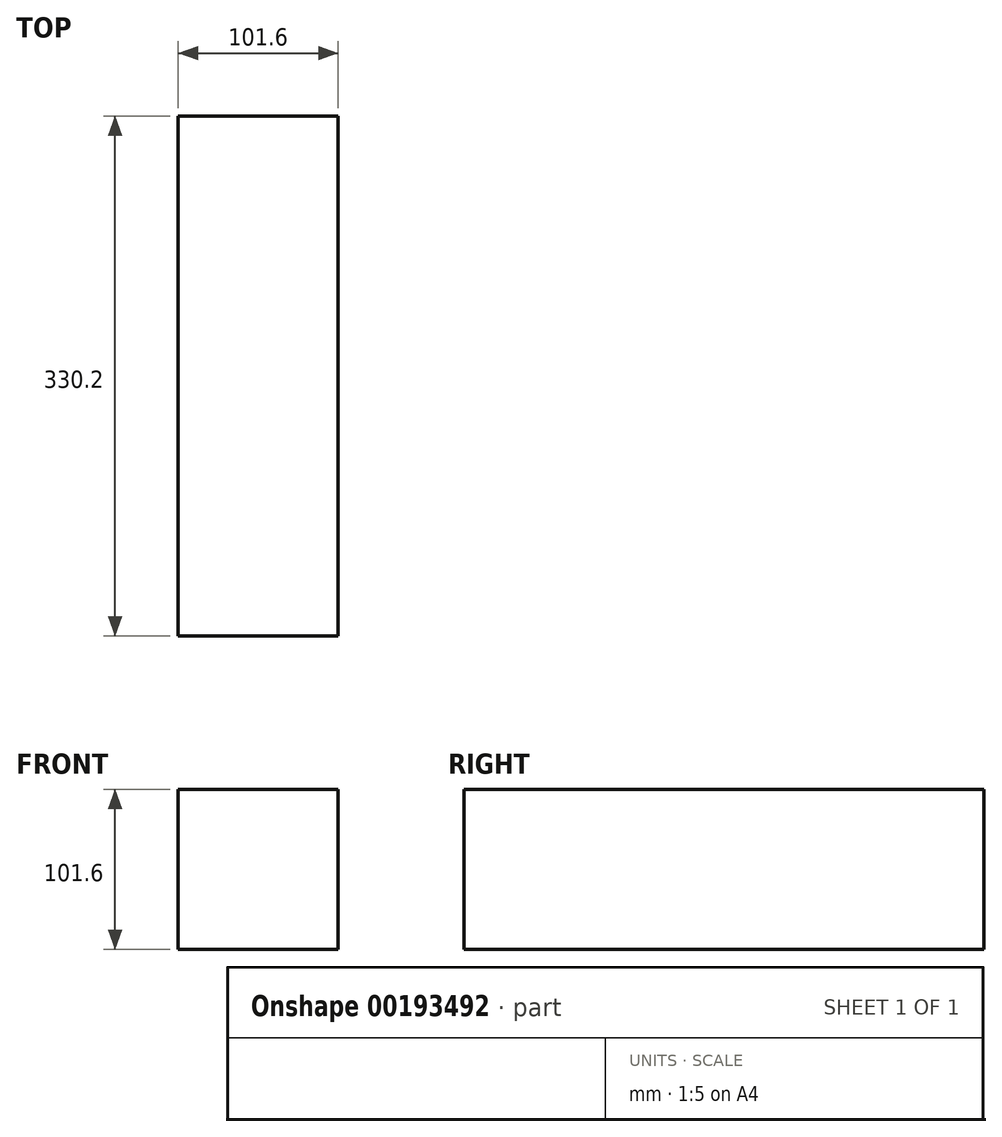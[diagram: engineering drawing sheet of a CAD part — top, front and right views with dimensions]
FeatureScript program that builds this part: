
annotation { "Feature Type Name" : "Feature", "Feature Type Description" : "" }
export const myFeature = defineFeature(function(context is Context, id is Id, definition is map)
    precondition{}
    {
        {
            var Q0;
            Q0=qCreatedBy(makeId("Top.planeOp"),FACE);
            var sketch = newSketch(context, id + "F0", { "sketchPlane" : qUnion([Q0])});
            skLineSegment(sketch, "E0.bottom", {"start": v(50.8, 38.1) * mm, "end": v(-50.8, 38.1) * mm});
            skLineSegment(sketch, "E0.top", {"start": v(50.8, -38.1) * mm, "end": v(-50.8, -38.1) * mm});
            skLineSegment(sketch, "E0.left", {"start": v(50.8, 38.1) * mm, "end": v(50.8, -38.1) * mm});
            skLineSegment(sketch, "E0.right", {"start": v(-50.8, 38.1) * mm, "end": v(-50.8, -38.1) * mm});
            skPoint(sketch, "E0.middle", {"position": v(0, 0) * mm});
            skSolve(sketch);
        }
        {
            var Q0;
            Q0 = qSketchRegion(id + "F0", true);
            extrude(context, id + "F1", {"entities" : qUnion([Q0]), "depth" : 25.4 * mm});
        }
        {
            var Q0;
            Q0=makeQuery(id+"F1.opExtrude","CAP_FACE",FACE,{"disambiguationData":[OSD([sQuery(id+"F0.wireOp",EDGE,"E0.bottom"),sQuery(id+"F0.wireOp",EDGE,"E0.top"),sQuery(id+"F0.wireOp",EDGE,"E0.left"),sQuery(id+"F0.wireOp",EDGE,"E0.right")])],"isStart":true});
            extrude(context, id + "F2", {"entities" : qUnion([Q0]), "operationType" : NewBodyOperationType.ADD, "depth" : 76.2 * mm});
        }
        {
            var Q0;
            {var subQ0=sQuery(id+"F0.wireOp",EDGE,"E0.top");Q0=makeQuery(id+"F2.boolean.opBoolean","MERGE",FACE,{"derivedFrom":[makeQuery(id+"F1.opExtrude","SWEPT_FACE",FACE,{"disambiguationData":[OSD([subQ0])]}),makeQuery(id+"F2.opExtrude","SWEPT_FACE",FACE,{"disambiguationData":[OSD([subQ0])]})]});}
            extrude(context, id + "F3", {"entities" : qUnion([Q0]), "operationType" : NewBodyOperationType.ADD, "depth" : 254 * mm});
        }
    });
